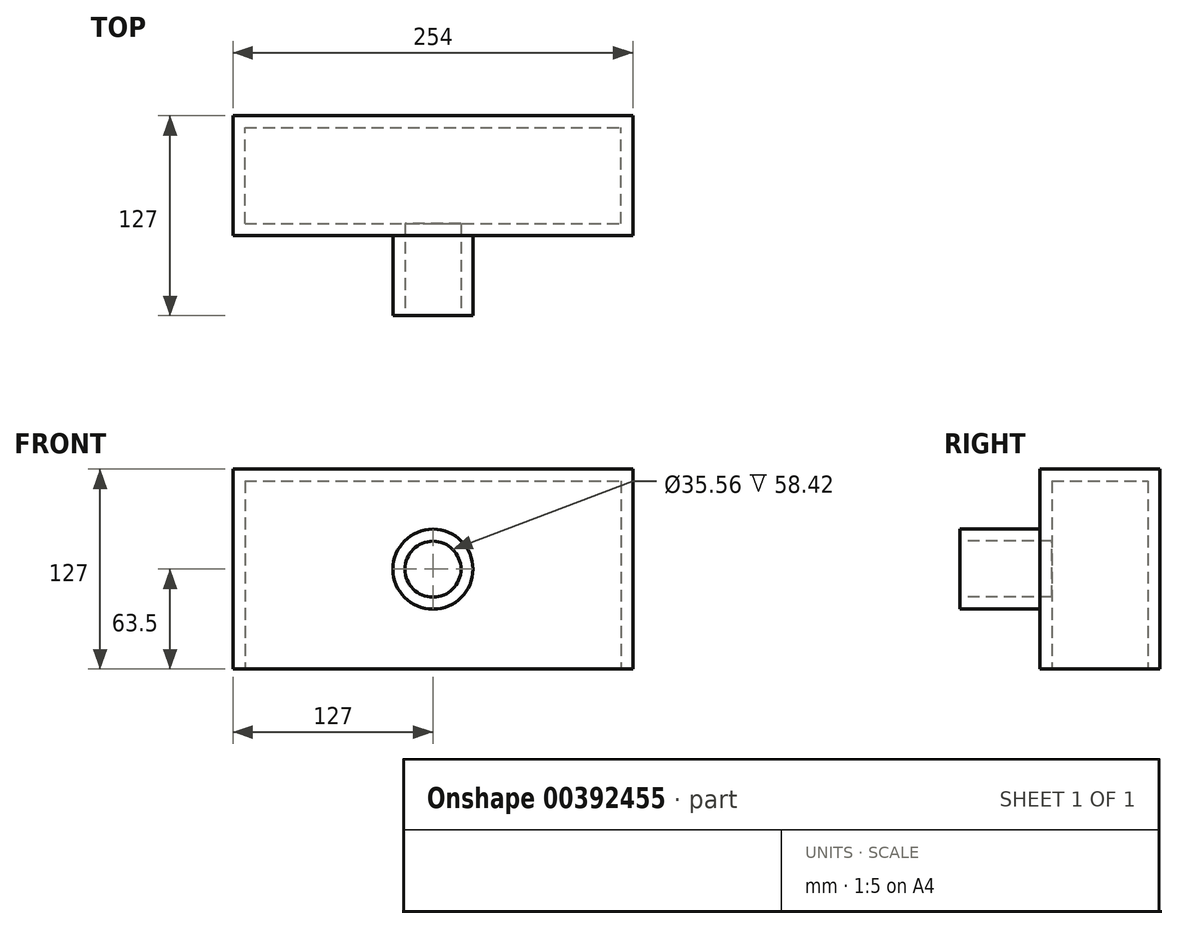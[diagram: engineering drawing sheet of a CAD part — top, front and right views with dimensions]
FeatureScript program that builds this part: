
annotation { "Feature Type Name" : "Feature", "Feature Type Description" : "" }
export const myFeature = defineFeature(function(context is Context, id is Id, definition is map)
    precondition{}
    {
        {
            var Q0;
            Q0=qCreatedBy(makeId("Front.planeOp"),FACE);
            var sketch = newSketch(context, id + "F0", { "sketchPlane" : qUnion([Q0])});
            skLineSegment(sketch, "E0.bottom", {"start": v(-127, 63.5) * mm, "end": v(127, 63.5) * mm});
            skLineSegment(sketch, "E0.top", {"start": v(-127, -63.5) * mm, "end": v(127, -63.5) * mm});
            skLineSegment(sketch, "E0.left", {"start": v(-127, 63.5) * mm, "end": v(-127, -63.5) * mm});
            skLineSegment(sketch, "E0.right", {"start": v(127, 63.5) * mm, "end": v(127, -63.5) * mm});
            skSolve(sketch);
        }
        {
            var Q0;
            Q0 = qSketchRegion(id + "F0", true);
            extrude(context, id + "F1", {"entities" : qUnion([Q0]), "depth" : 76.2 * mm});
        }
        {
            var Q0;
            Q0=qCreatedBy(makeId("Top.planeOp"),FACE);
            var sketch = newSketch(context, id + "F2", { "sketchPlane" : qUnion([Q0])});
            skLineSegment(sketch, "E1.bottom", {"start": v(0, -127) * mm, "end": v(25.4, -127) * mm});
            skLineSegment(sketch, "E1.top", {"start": v(0, -76.2) * mm, "end": v(25.4, -76.2) * mm});
            skLineSegment(sketch, "E1.left", {"start": v(0, -127) * mm, "end": v(0, -76.2) * mm});
            skLineSegment(sketch, "E1.right", {"start": v(25.4, -127) * mm, "end": v(25.4, -76.2) * mm});
            skSolve(sketch);
        }
        {
            var Q0;
            Q0 = qSketchRegion(id + "F2", true);
            var Q1;
            Q1=sQuery(id+"F2.wireOp",EDGE,"E1.left");
            revolve(context, id + "F3", {"operationType" : NewBodyOperationType.ADD, "entities" : qUnion([Q0]), "axis" : qUnion([Q1]), "revolveType" : RevolveType.FULL});
        }
        {
            var Q0;
            Q0=makeQuery(id+"F3.opRevolve","SWEPT_FACE",FACE,{"disambiguationData":[OSD([sQuery(id+"F2.wireOp",EDGE,"E1.bottom")])]});
            var Q1;
            Q1=makeQuery(id+"F1.opExtrude","SWEPT_FACE",FACE,{"disambiguationData":[OSD([sQuery(id+"F0.wireOp",EDGE,"E0.top")])]});
            shell(context, id + "F4", {"entities" : qUnion([Q0, Q1]), "thickness" : 7.62 * mm});
        }
    });
